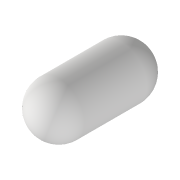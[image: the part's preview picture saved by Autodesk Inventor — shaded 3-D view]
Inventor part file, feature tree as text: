
AUTODESK INVENTOR PART (.ipt)
format: ipt  version: 2022 (Build 260153000, 153)  size: 103,936 bytes
history: native  units: mm
features: extrude x1, fillet x1, sketch x1
ambient origin geometry x8: Origin, YZ Plane, XZ Plane, XY Plane, X Axis, Y Axis, Z Axis, Center Point
bodies: Volumenkörper1 (feature_tree)
feature tree (3):
  extrude  "Extrusion1"  Depth=5.0mm TaperAngle=0.0deg
  fillet  "Rundung1"  Radius=5.0mm
  sketch  "Skizze1"  dims[d0=10.0mm d1=22.0mm d2=0.0mm d3=5.0mm]
